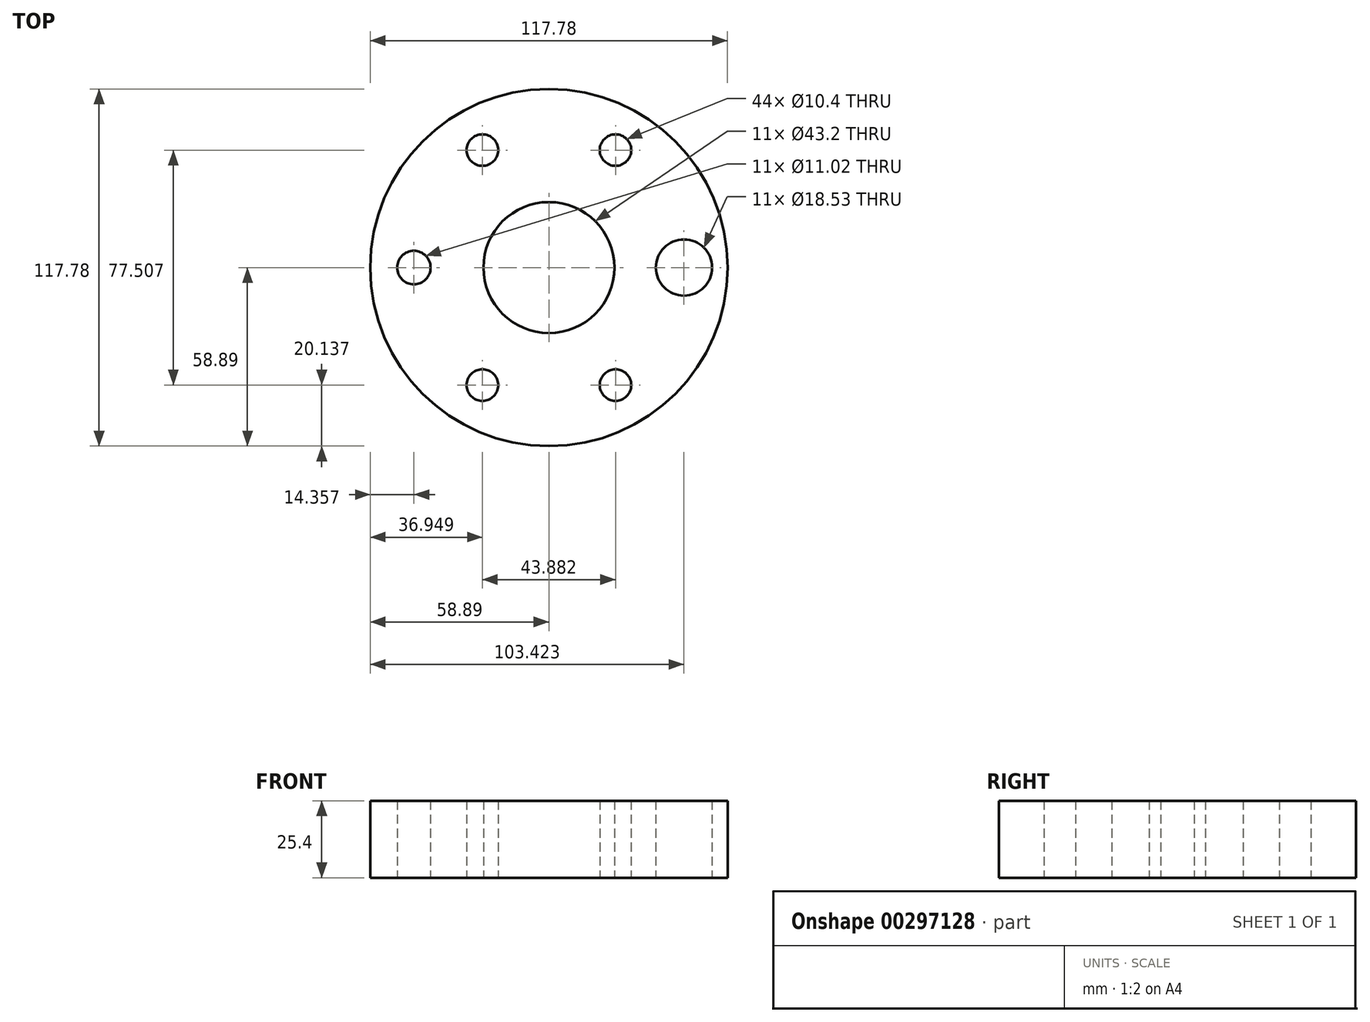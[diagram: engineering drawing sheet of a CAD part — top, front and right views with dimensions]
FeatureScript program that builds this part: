
annotation { "Feature Type Name" : "Feature", "Feature Type Description" : "" }
export const myFeature = defineFeature(function(context is Context, id is Id, definition is map)
    precondition{}
    {
        {
            var Q0;
            Q0=qCreatedBy(makeId("Top.planeOp"),FACE);
            var sketch = newSketch(context, id + "F0", { "sketchPlane" : qUnion([Q0])});
            skCircle(sketch, "E0", {"center": v(0, 0) * mm, "radius": 58.9 * mm});
            skCircle(sketch, "E1", {"center": v(0, 0) * mm, "radius": 21.6 * mm});
            skCircle(sketch, "E2", {"center": v(0, 0) * mm, "radius": 44.53 * mm, "construction": true});
            skCircle(sketch, "E3", {"center": v(-21.94, 38.75) * mm, "radius": 5.2 * mm});
            skCircle(sketch, "E4", {"center": v(21.94, 38.75) * mm, "radius": 5.2 * mm});
            skCircle(sketch, "E5", {"center": v(-44.53, 0) * mm, "radius": 5.51 * mm});
            skCircle(sketch, "E6", {"center": v(44.53, 0) * mm, "radius": 9.27 * mm});
            skCircle(sketch, "E7", {"center": v(21.94, -38.75) * mm, "radius": 5.2 * mm});
            skCircle(sketch, "E8", {"center": v(-21.94, -38.75) * mm, "radius": 5.2 * mm});
            skSolve(sketch);
        }
        {
            var Q0;
            Q0=makeQuery(id+"F0.imprint","IMPRINT",FACE,{"disambiguationData":[TD([[makeQuery(id+"F0.imprint","IMPRINT",EDGE,{"derivedFrom":sQuery(id+"F0.wireOp",EDGE,"E0")}),1.0]])]});
            extrude(context, id + "F1", {"entities" : qUnion([Q0]), "depth" : 25.4 * mm, "hasSecondDirectionDraft" : true, "secondDirectionDraftAngle" : 3 * degree});
        }
    });
